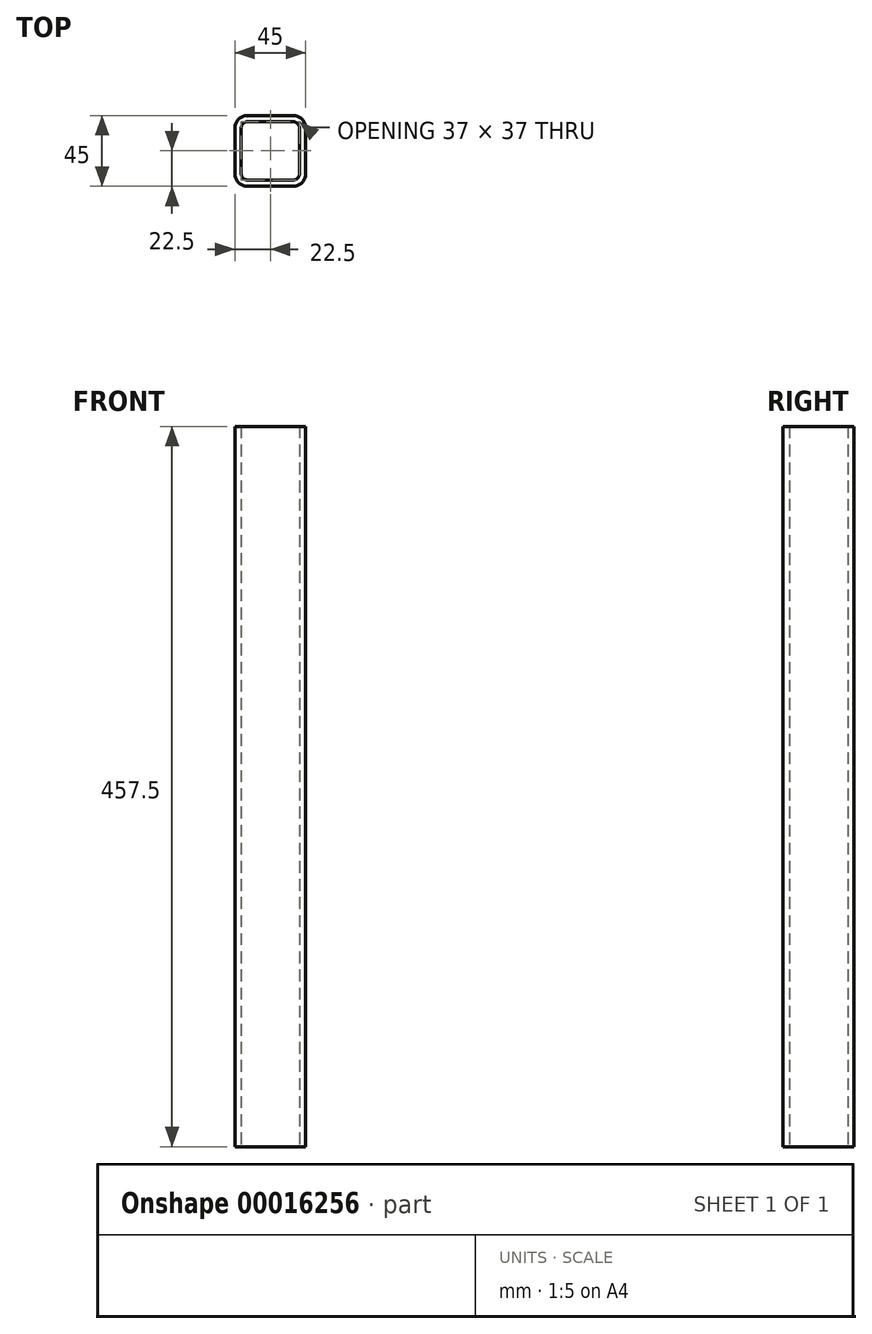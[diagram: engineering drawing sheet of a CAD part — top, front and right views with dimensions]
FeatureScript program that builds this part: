
annotation { "Feature Type Name" : "Feature", "Feature Type Description" : "" }
export const myFeature = defineFeature(function(context is Context, id is Id, definition is map)
    precondition{}
    {
        {
            var Q0;
            Q0=qCreatedBy(makeId("Top.planeOp"), FACE);
            var sketch = newSketch(context, id + "F0", { "sketchPlane" : qUnion([Q0])});
            skLineSegment(sketch, "E0.bottom", {"start": v(-14.5, 22.5) * mm, "end": v(14.5, 22.5) * mm});
            skLineSegment(sketch, "E0.top", {"start": v(-14.5, -22.5) * mm, "end": v(14.5, -22.5) * mm});
            skLineSegment(sketch, "E0.left", {"start": v(-22.5, 14.5) * mm, "end": v(-22.5, -14.5) * mm});
            skLineSegment(sketch, "E0.right", {"start": v(22.5, 14.5) * mm, "end": v(22.5, -14.5) * mm});
            skPoint(sketch, "E1.visualSharp", {"position": v(22.5, -22.5) * mm});
            skArc(sketch, "E1.filletArc", {"start": v(14.5, -22.5) * mm, "mid": v(20.16, -20.16) * mm, "end": v(22.5, -14.5) * mm});
            skPoint(sketch, "E2.visualSharp", {"position": v(22.5, 22.5) * mm});
            skArc(sketch, "E2.filletArc", {"start": v(22.5, 14.5) * mm, "mid": v(20.16, 20.16) * mm, "end": v(14.5, 22.5) * mm});
            skPoint(sketch, "E3.visualSharp", {"position": v(-22.5, 22.5) * mm});
            skArc(sketch, "E3.filletArc", {"start": v(-14.5, 22.5) * mm, "mid": v(-20.16, 20.16) * mm, "end": v(-22.5, 14.5) * mm});
            skPoint(sketch, "E4.visualSharp", {"position": v(-22.5, -22.5) * mm});
            skArc(sketch, "E4.filletArc", {"start": v(-22.5, -14.5) * mm, "mid": v(-20.16, -20.16) * mm, "end": v(-14.5, -22.5) * mm});
            skArc(sketch, "E5.0", {"start": v(-18.5, -14.5) * mm, "mid": v(-17.33, -17.33) * mm, "end": v(-14.5, -18.5) * mm});
            skLineSegment(sketch, "E5.1", {"start": v(-14.5, -18.5) * mm, "end": v(14.5, -18.5) * mm});
            skArc(sketch, "E5.2", {"start": v(14.5, -18.5) * mm, "mid": v(17.33, -17.33) * mm, "end": v(18.5, -14.5) * mm});
            skLineSegment(sketch, "E5.3", {"start": v(18.5, 14.5) * mm, "end": v(18.5, -14.5) * mm});
            skArc(sketch, "E5.4", {"start": v(18.5, 14.5) * mm, "mid": v(17.33, 17.33) * mm, "end": v(14.5, 18.5) * mm});
            skLineSegment(sketch, "E5.5", {"start": v(-14.5, 18.5) * mm, "end": v(14.5, 18.5) * mm});
            skArc(sketch, "E5.6", {"start": v(-14.5, 18.5) * mm, "mid": v(-17.33, 17.33) * mm, "end": v(-18.5, 14.5) * mm});
            skLineSegment(sketch, "E5.7", {"start": v(-18.5, 14.5) * mm, "end": v(-18.5, -14.5) * mm});
            skSolve(sketch);
        }
        {
            var Q0;
            Q0 = qSketchRegion(id + "F0", true);
            extrude(context, id + "F1", {"entities" : qUnion([Q0]), "depth" : 457.5 * mm, "offsetDistance" : 25 * mm});
        }
    });
